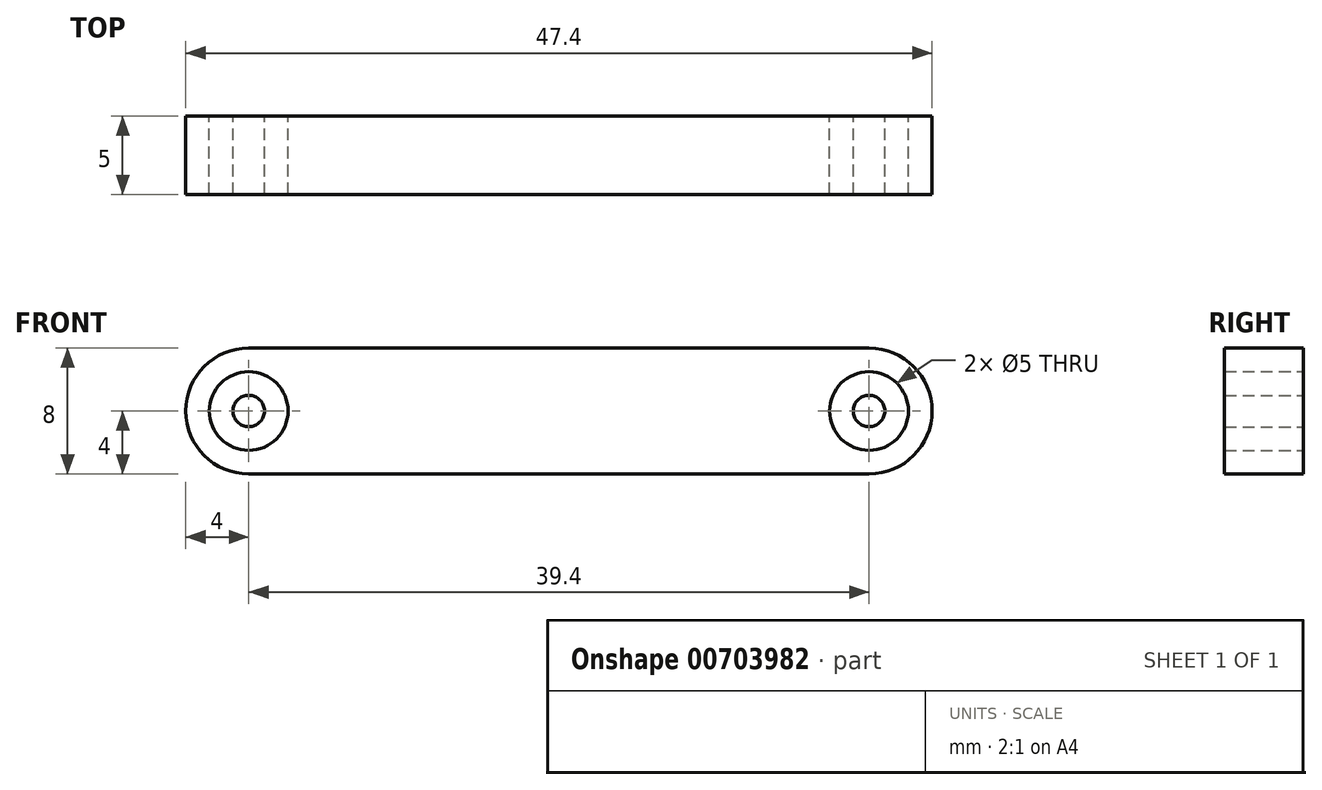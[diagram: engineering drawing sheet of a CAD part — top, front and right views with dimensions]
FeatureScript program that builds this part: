
annotation { "Feature Type Name" : "Feature", "Feature Type Description" : "" }
export const myFeature = defineFeature(function(context is Context, id is Id, definition is map)
    precondition{}
    {
        {
            var Q0;
            Q0=qCreatedBy(makeId("Front.planeOp"),FACE);
            var sketch = newSketch(context, id + "F0", { "sketchPlane" : qUnion([Q0])});
            skLineSegment(sketch, "E0.bottom", {"start": v(0, 0) * mm, "end": v(39.4, 0) * mm});
            skLineSegment(sketch, "E0.top", {"start": v(0, 8) * mm, "end": v(39.4, 8) * mm});
            skArc(sketch, "E1", {"start": v(39.4, 0) * mm, "mid": v(43.4, 4) * mm, "end": v(39.4, 8) * mm});
            skArc(sketch, "E2", {"start": v(0, 8) * mm, "mid": v(-4, 4) * mm, "end": v(0, 0) * mm});
            skCircle(sketch, "E3", {"center": v(0, 4) * mm, "radius": 2.5 * mm});
            skCircle(sketch, "E4", {"center": v(0, 4) * mm, "radius": 1 * mm});
            skCircle(sketch, "E5", {"center": v(39.4, 4) * mm, "radius": 2.5 * mm});
            skCircle(sketch, "E6", {"center": v(39.4, 4) * mm, "radius": 1 * mm});
            skSolve(sketch);
        }
        {
            var Q0;
            Q0 = qSketchRegion(id + "F0", true);
            var Q1;
            Q1=makeQuery(id+"F0.imprint","IMPRINT",FACE,{"disambiguationData":[TD([[makeQuery(id+"F0.imprint","IMPRINT",EDGE,{"derivedFrom":sQuery(id+"F0.wireOp",EDGE,"E4")}),1.0]])]});
            var Q2;
            Q2=makeQuery(id+"F0.imprint","IMPRINT",FACE,{"disambiguationData":[TD([[makeQuery(id+"F0.imprint","IMPRINT",EDGE,{"derivedFrom":sQuery(id+"F0.wireOp",EDGE,"E6")}),1.0]])]});
            extrude(context, id + "F1", {"entities" : qUnion([Q0, Q1, Q2]), "depth" : 5 * mm, "offsetDistance" : 25 * mm});
        }
    });
